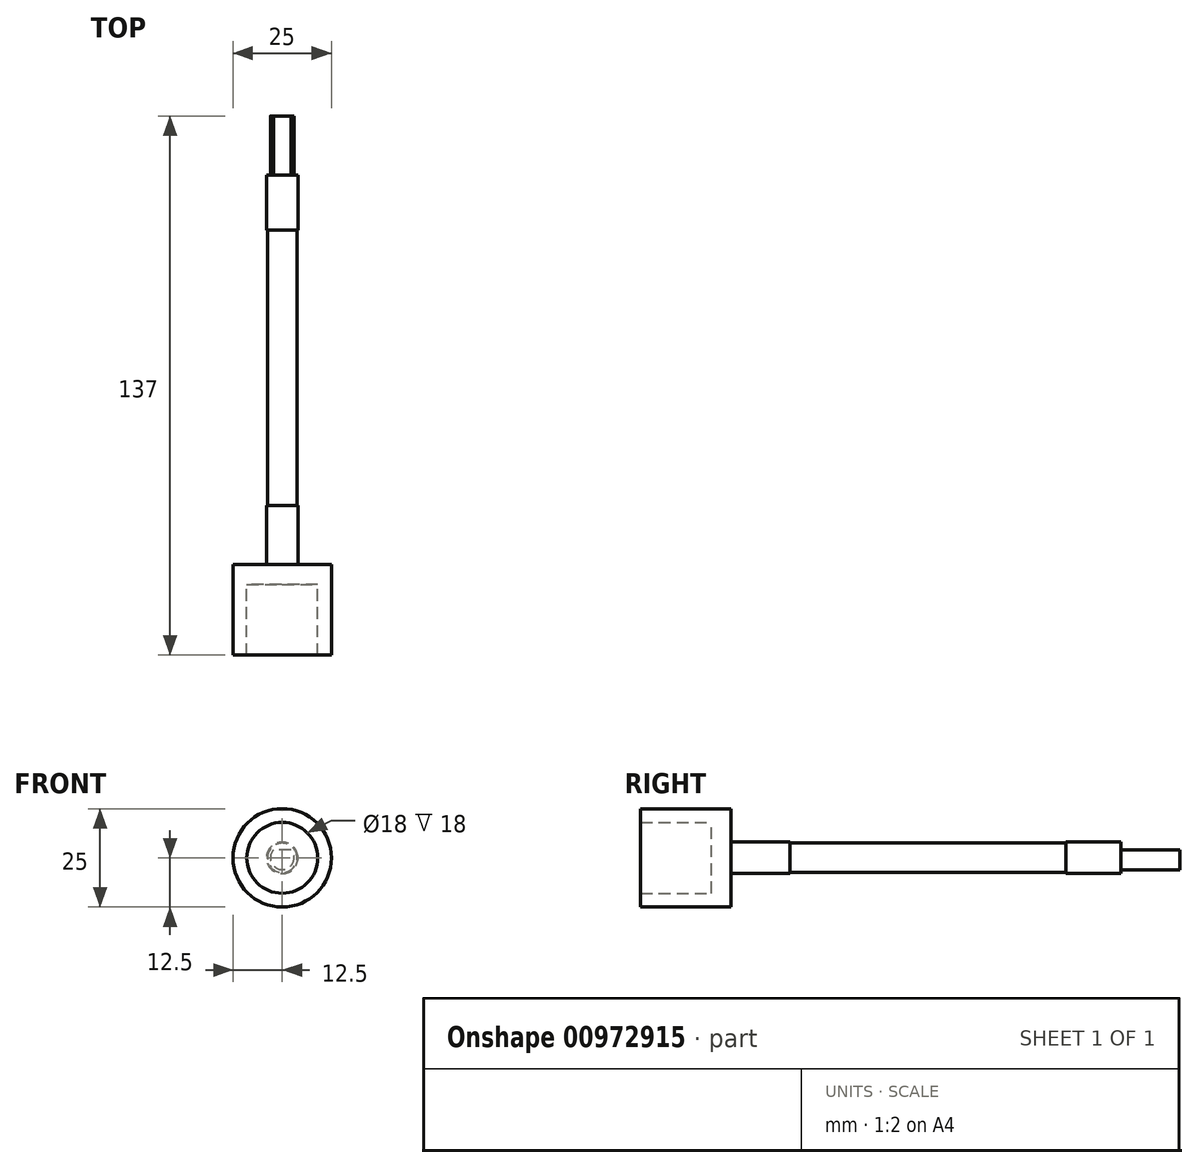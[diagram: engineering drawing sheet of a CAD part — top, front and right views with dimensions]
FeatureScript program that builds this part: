
annotation { "Feature Type Name" : "Feature", "Feature Type Description" : "" }
export const myFeature = defineFeature(function(context is Context, id is Id, definition is map)
    precondition{}
    {
        {
            var Q0;
            Q0=qCreatedBy(makeId("Front.planeOp"),FACE);
            var sketch = newSketch(context, id + "F0", { "sketchPlane" : qUnion([Q0])});
            skCircle(sketch, "E0", {"center": v(0, 0) * mm, "radius": 12.5 * mm});
            skSolve(sketch);
        }
        {
            var Q0;
            Q0 = qSketchRegion(id + "F0", true);
            extrude(context, id + "F1", {"entities" : qUnion([Q0]), "depth" : 5 * mm, "offsetDistance" : 25 * mm});
        }
        {
            var Q0;
            Q0=makeQuery(id+"F1.opExtrude","CAP_FACE",FACE,{"disambiguationData":[OSD([sQuery(id+"F0.wireOp",EDGE,"E0")])],"isStart":false});
            var sketch = newSketch(context, id + "F2", { "sketchPlane" : qUnion([Q0])});
            skCircle(sketch, "E1", {"center": v(0, 0) * mm, "radius": 9 * mm});
            skCircle(sketch, "E2", {"center": v(0, 0) * mm, "radius": 12.5 * mm});
            skSolve(sketch);
        }
        {
            var Q0;
            Q0 = qSketchRegion(id + "F2", true);
            extrude(context, id + "F3", {"entities" : qUnion([Q0]), "operationType" : NewBodyOperationType.ADD, "depth" : 18 * mm, "offsetDistance" : 25 * mm});
        }
        {
            var Q0;
            Q0=makeQuery(id+"F1.opExtrude","CAP_FACE",FACE,{"disambiguationData":[OSD([sQuery(id+"F0.wireOp",EDGE,"E0")])],"isStart":true});
            var sketch = newSketch(context, id + "F4", { "sketchPlane" : qUnion([Q0])});
            skCircle(sketch, "E3", {"center": v(0, 0) * mm, "radius": 4 * mm});
            skSolve(sketch);
        }
        {
            var Q0;
            Q0 = qSketchRegion(id + "F4", true);
            extrude(context, id + "F5", {"entities" : qUnion([Q0]), "operationType" : NewBodyOperationType.ADD, "depth" : 15 * mm, "offsetDistance" : 25 * mm});
        }
        {
            var Q0;
            Q0=makeQuery(id+"F5.opExtrude","CAP_FACE",FACE,{"disambiguationData":[OSD([sQuery(id+"F4.wireOp",EDGE,"E3")])],"isStart":false});
            var sketch = newSketch(context, id + "F6", { "sketchPlane" : qUnion([Q0])});
            skCircle(sketch, "E4", {"center": v(0, 0) * mm, "radius": 3.75 * mm});
            skSolve(sketch);
        }
        {
            var Q0;
            Q0 = qSketchRegion(id + "F6", true);
            extrude(context, id + "F7", {"entities" : qUnion([Q0]), "operationType" : NewBodyOperationType.ADD, "depth" : 70 * mm, "offsetDistance" : 25 * mm});
        }
        {
            var Q0;
            Q0=makeQuery(id+"F7.opExtrude","CAP_FACE",FACE,{"disambiguationData":[OSD([sQuery(id+"F6.wireOp",EDGE,"E4")])],"isStart":false});
            var sketch = newSketch(context, id + "F8", { "sketchPlane" : qUnion([Q0])});
            skCircle(sketch, "E5", {"center": v(0, 0) * mm, "radius": 4 * mm});
            skSolve(sketch);
        }
        {
            var Q0;
            Q0 = qSketchRegion(id + "F8", true);
            extrude(context, id + "F9", {"entities" : qUnion([Q0]), "operationType" : NewBodyOperationType.ADD, "depth" : 14 * mm, "offsetDistance" : 25 * mm});
        }
        {
            var Q0;
            Q0=makeQuery(id+"F9.opExtrude","CAP_FACE",FACE,{"disambiguationData":[OSD([sQuery(id+"F8.wireOp",EDGE,"E5")])],"isStart":false});
            var sketch = newSketch(context, id + "F10", { "sketchPlane" : qUnion([Q0])});
            skArc(sketch, "E6", {"start": v(-2.24, 2) * mm, "mid": v(0, -3) * mm, "end": v(2.24, 2) * mm});
            skLineSegment(sketch, "E7", {"start": v(-2.24, 2) * mm, "end": v(2.24, 2) * mm});
            skSolve(sketch);
        }
        {
            var Q0;
            Q0 = qSketchRegion(id + "F10", true);
            extrude(context, id + "F11", {"entities" : qUnion([Q0]), "operationType" : NewBodyOperationType.ADD, "depth" : 15 * mm, "offsetDistance" : 25 * mm});
        }
    });
